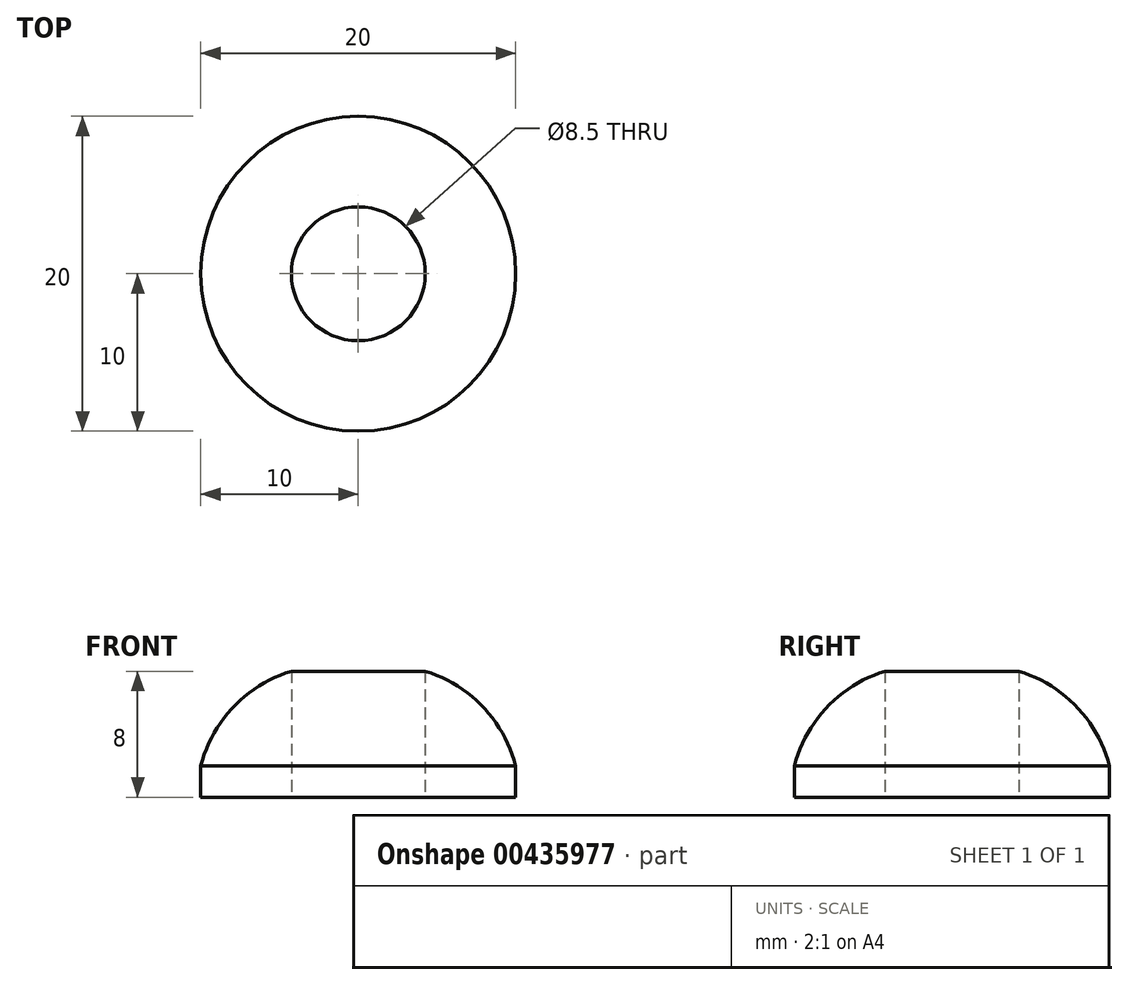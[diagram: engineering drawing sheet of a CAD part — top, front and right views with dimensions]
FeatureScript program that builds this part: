
annotation { "Feature Type Name" : "Feature", "Feature Type Description" : "" }
export const myFeature = defineFeature(function(context is Context, id is Id, definition is map)
    precondition{}
    {
        {
            var Q0;
            Q0=qCreatedBy(makeId("Front.planeOp"),FACE);
            var sketch = newSketch(context, id + "F0", { "sketchPlane" : qUnion([Q0])});
            skLineSegment(sketch, "E0", {"start": v(0, 0) * mm, "end": v(-4.25, 0) * mm, "construction": true});
            skLineSegment(sketch, "E1", {"start": v(-4.25, 0) * mm, "end": v(-10, 0) * mm});
            skLineSegment(sketch, "E2", {"start": v(-10, 0) * mm, "end": v(-10, 2) * mm});
            skLineSegment(sketch, "E3", {"start": v(-4.25, 0) * mm, "end": v(-4.25, 8) * mm});
            skArc(sketch, "E4", {"start": v(-4.25, 8) * mm, "mid": v(-7.9, 5.75) * mm, "end": v(-10, 2) * mm});
            skLineSegment(sketch, "E5", {"start": v(0, 0) * mm, "end": v(0, 31.13) * mm, "construction": true});
            skSolve(sketch);
        }
        {
            var Q0;
            Q0=makeQuery(id+"F0.imprint","IMPRINT",FACE,{"disambiguationData":[TD([[makeQuery(id+"F0.imprint","IMPRINT",EDGE,{"derivedFrom":sQuery(id+"F0.wireOp",EDGE,"E1")}),-1.0]])]});
            var Q1;
            Q1=sQuery(id+"F0.wireOp",EDGE,"E5");
            revolve(context, id + "F1", {"entities" : qUnion([Q0]), "axis" : qUnion([Q1]), "revolveType" : RevolveType.FULL});
        }
    });
